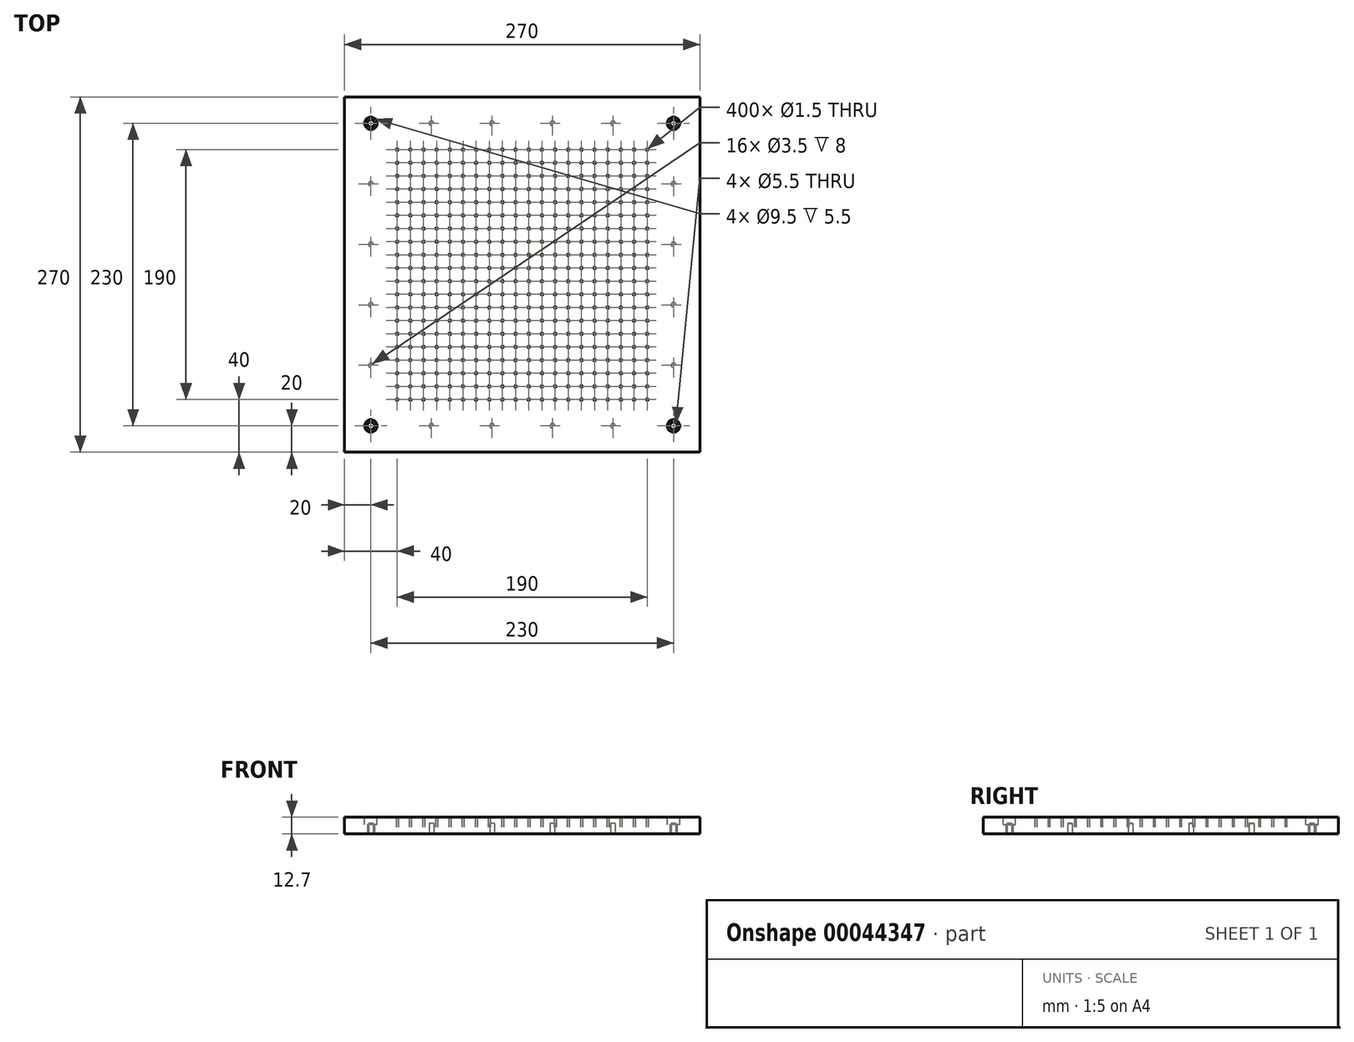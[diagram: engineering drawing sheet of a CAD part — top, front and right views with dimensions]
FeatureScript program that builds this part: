
annotation { "Feature Type Name" : "Feature", "Feature Type Description" : "" }
export const myFeature = defineFeature(function(context is Context, id is Id, definition is map)
    precondition{}
    {
        {
            var Q0;
            Q0=qCreatedBy(makeId("Top.planeOp"),FACE);
            var sketch = newSketch(context, id + "F0", { "sketchPlane" : qUnion([Q0])});
            skLineSegment(sketch, "E0.bottom", {"start": v(0, 0) * mm, "end": v(270, 0) * mm});
            skLineSegment(sketch, "E0.top", {"start": v(0, 270) * mm, "end": v(270, 270) * mm});
            skLineSegment(sketch, "E0.left", {"start": v(0, 0) * mm, "end": v(0, 270) * mm});
            skLineSegment(sketch, "E0.right", {"start": v(270, 0) * mm, "end": v(270, 270) * mm});
            skCircle(sketch, "E1", {"center": v(20, 250) * mm, "radius": 2.75 * mm});
            skCircle(sketch, "E2", {"center": v(250, 250) * mm, "radius": 2.75 * mm});
            skCircle(sketch, "E3", {"center": v(20, 20) * mm, "radius": 2.75 * mm});
            skCircle(sketch, "E4", {"center": v(250, 20) * mm, "radius": 2.75 * mm});
            skCircle(sketch, "E5", {"center": v(230, 40) * mm, "radius": 0.75 * mm});
            skCircle(sketch, "E6.0.1.0", {"center": v(230, 50) * mm, "radius": 0.75 * mm});
            skCircle(sketch, "E6.0.2.0", {"center": v(230, 60) * mm, "radius": 0.75 * mm});
            skCircle(sketch, "E6.0.3.0", {"center": v(230, 70) * mm, "radius": 0.75 * mm});
            skCircle(sketch, "E6.0.4.0", {"center": v(230, 80) * mm, "radius": 0.75 * mm});
            skCircle(sketch, "E6.0.5.0", {"center": v(230, 90) * mm, "radius": 0.75 * mm});
            skCircle(sketch, "E6.0.6.0", {"center": v(230, 100) * mm, "radius": 0.75 * mm});
            skCircle(sketch, "E6.0.7.0", {"center": v(230, 110) * mm, "radius": 0.75 * mm});
            skCircle(sketch, "E6.0.8.0", {"center": v(230, 120) * mm, "radius": 0.75 * mm});
            skCircle(sketch, "E6.0.9.0", {"center": v(230, 130) * mm, "radius": 0.75 * mm});
            skCircle(sketch, "E6.0.10.0", {"center": v(230, 140) * mm, "radius": 0.75 * mm});
            skCircle(sketch, "E6.0.11.0", {"center": v(230, 150) * mm, "radius": 0.75 * mm});
            skCircle(sketch, "E6.0.12.0", {"center": v(230, 160) * mm, "radius": 0.75 * mm});
            skCircle(sketch, "E6.0.13.0", {"center": v(230, 170) * mm, "radius": 0.75 * mm});
            skCircle(sketch, "E6.0.14.0", {"center": v(230, 180) * mm, "radius": 0.75 * mm});
            skCircle(sketch, "E6.0.15.0", {"center": v(230, 190) * mm, "radius": 0.75 * mm});
            skCircle(sketch, "E6.1.0.0", {"center": v(220, 40) * mm, "radius": 0.75 * mm});
            skCircle(sketch, "E6.1.1.0", {"center": v(220, 50) * mm, "radius": 0.75 * mm});
            skCircle(sketch, "E6.1.2.0", {"center": v(220, 60) * mm, "radius": 0.75 * mm});
            skCircle(sketch, "E6.1.3.0", {"center": v(220, 70) * mm, "radius": 0.75 * mm});
            skCircle(sketch, "E6.1.4.0", {"center": v(220, 80) * mm, "radius": 0.75 * mm});
            skCircle(sketch, "E6.1.5.0", {"center": v(220, 90) * mm, "radius": 0.75 * mm});
            skCircle(sketch, "E6.1.6.0", {"center": v(220, 100) * mm, "radius": 0.75 * mm});
            skCircle(sketch, "E6.1.7.0", {"center": v(220, 110) * mm, "radius": 0.75 * mm});
            skCircle(sketch, "E6.1.8.0", {"center": v(220, 120) * mm, "radius": 0.75 * mm});
            skCircle(sketch, "E6.1.9.0", {"center": v(220, 130) * mm, "radius": 0.75 * mm});
            skCircle(sketch, "E6.1.10.0", {"center": v(220, 140) * mm, "radius": 0.75 * mm});
            skCircle(sketch, "E6.1.11.0", {"center": v(220, 150) * mm, "radius": 0.75 * mm});
            skCircle(sketch, "E6.1.12.0", {"center": v(220, 160) * mm, "radius": 0.75 * mm});
            skCircle(sketch, "E6.1.13.0", {"center": v(220, 170) * mm, "radius": 0.75 * mm});
            skCircle(sketch, "E6.1.14.0", {"center": v(220, 180) * mm, "radius": 0.75 * mm});
            skCircle(sketch, "E6.1.15.0", {"center": v(220, 190) * mm, "radius": 0.75 * mm});
            skCircle(sketch, "E6.2.0.0", {"center": v(210, 40) * mm, "radius": 0.75 * mm});
            skCircle(sketch, "E6.2.1.0", {"center": v(210, 50) * mm, "radius": 0.75 * mm});
            skCircle(sketch, "E6.2.2.0", {"center": v(210, 60) * mm, "radius": 0.75 * mm});
            skCircle(sketch, "E6.2.3.0", {"center": v(210, 70) * mm, "radius": 0.75 * mm});
            skCircle(sketch, "E6.2.4.0", {"center": v(210, 80) * mm, "radius": 0.75 * mm});
            skCircle(sketch, "E6.2.5.0", {"center": v(210, 90) * mm, "radius": 0.75 * mm});
            skCircle(sketch, "E6.2.6.0", {"center": v(210, 100) * mm, "radius": 0.75 * mm});
            skCircle(sketch, "E6.2.7.0", {"center": v(210, 110) * mm, "radius": 0.75 * mm});
            skCircle(sketch, "E6.2.8.0", {"center": v(210, 120) * mm, "radius": 0.75 * mm});
            skCircle(sketch, "E6.2.9.0", {"center": v(210, 130) * mm, "radius": 0.75 * mm});
            skCircle(sketch, "E6.2.10.0", {"center": v(210, 140) * mm, "radius": 0.75 * mm});
            skCircle(sketch, "E6.2.11.0", {"center": v(210, 150) * mm, "radius": 0.75 * mm});
            skCircle(sketch, "E6.2.12.0", {"center": v(210, 160) * mm, "radius": 0.75 * mm});
            skCircle(sketch, "E6.2.13.0", {"center": v(210, 170) * mm, "radius": 0.75 * mm});
            skCircle(sketch, "E6.2.14.0", {"center": v(210, 180) * mm, "radius": 0.75 * mm});
            skCircle(sketch, "E6.2.15.0", {"center": v(210, 190) * mm, "radius": 0.75 * mm});
            skCircle(sketch, "E6.3.0.0", {"center": v(200, 40) * mm, "radius": 0.75 * mm});
            skCircle(sketch, "E6.3.1.0", {"center": v(200, 50) * mm, "radius": 0.75 * mm});
            skCircle(sketch, "E6.3.2.0", {"center": v(200, 60) * mm, "radius": 0.75 * mm});
            skCircle(sketch, "E6.3.3.0", {"center": v(200, 70) * mm, "radius": 0.75 * mm});
            skCircle(sketch, "E6.3.4.0", {"center": v(200, 80) * mm, "radius": 0.75 * mm});
            skCircle(sketch, "E6.3.5.0", {"center": v(200, 90) * mm, "radius": 0.75 * mm});
            skCircle(sketch, "E6.3.6.0", {"center": v(200, 100) * mm, "radius": 0.75 * mm});
            skCircle(sketch, "E6.3.7.0", {"center": v(200, 110) * mm, "radius": 0.75 * mm});
            skCircle(sketch, "E6.3.8.0", {"center": v(200, 120) * mm, "radius": 0.75 * mm});
            skCircle(sketch, "E6.3.9.0", {"center": v(200, 130) * mm, "radius": 0.75 * mm});
            skCircle(sketch, "E6.3.10.0", {"center": v(200, 140) * mm, "radius": 0.75 * mm});
            skCircle(sketch, "E6.3.11.0", {"center": v(200, 150) * mm, "radius": 0.75 * mm});
            skCircle(sketch, "E6.3.12.0", {"center": v(200, 160) * mm, "radius": 0.75 * mm});
            skCircle(sketch, "E6.3.13.0", {"center": v(200, 170) * mm, "radius": 0.75 * mm});
            skCircle(sketch, "E6.3.14.0", {"center": v(200, 180) * mm, "radius": 0.75 * mm});
            skCircle(sketch, "E6.3.15.0", {"center": v(200, 190) * mm, "radius": 0.75 * mm});
            skCircle(sketch, "E6.4.0.0", {"center": v(190, 40) * mm, "radius": 0.75 * mm});
            skCircle(sketch, "E6.4.1.0", {"center": v(190, 50) * mm, "radius": 0.75 * mm});
            skCircle(sketch, "E6.4.2.0", {"center": v(190, 60) * mm, "radius": 0.75 * mm});
            skCircle(sketch, "E6.4.3.0", {"center": v(190, 70) * mm, "radius": 0.75 * mm});
            skCircle(sketch, "E6.4.4.0", {"center": v(190, 80) * mm, "radius": 0.75 * mm});
            skCircle(sketch, "E6.4.5.0", {"center": v(190, 90) * mm, "radius": 0.75 * mm});
            skCircle(sketch, "E6.4.6.0", {"center": v(190, 100) * mm, "radius": 0.75 * mm});
            skCircle(sketch, "E6.4.7.0", {"center": v(190, 110) * mm, "radius": 0.75 * mm});
            skCircle(sketch, "E6.4.8.0", {"center": v(190, 120) * mm, "radius": 0.75 * mm});
            skCircle(sketch, "E6.4.9.0", {"center": v(190, 130) * mm, "radius": 0.75 * mm});
            skCircle(sketch, "E6.4.10.0", {"center": v(190, 140) * mm, "radius": 0.75 * mm});
            skCircle(sketch, "E6.4.11.0", {"center": v(190, 150) * mm, "radius": 0.75 * mm});
            skCircle(sketch, "E6.4.12.0", {"center": v(190, 160) * mm, "radius": 0.75 * mm});
            skCircle(sketch, "E6.4.13.0", {"center": v(190, 170) * mm, "radius": 0.75 * mm});
            skCircle(sketch, "E6.4.14.0", {"center": v(190, 180) * mm, "radius": 0.75 * mm});
            skCircle(sketch, "E6.4.15.0", {"center": v(190, 190) * mm, "radius": 0.75 * mm});
            skCircle(sketch, "E6.5.0.0", {"center": v(180, 40) * mm, "radius": 0.75 * mm});
            skCircle(sketch, "E6.5.1.0", {"center": v(180, 50) * mm, "radius": 0.75 * mm});
            skCircle(sketch, "E6.5.2.0", {"center": v(180, 60) * mm, "radius": 0.75 * mm});
            skCircle(sketch, "E6.5.3.0", {"center": v(180, 70) * mm, "radius": 0.75 * mm});
            skCircle(sketch, "E6.5.4.0", {"center": v(180, 80) * mm, "radius": 0.75 * mm});
            skCircle(sketch, "E6.5.5.0", {"center": v(180, 90) * mm, "radius": 0.75 * mm});
            skCircle(sketch, "E6.5.6.0", {"center": v(180, 100) * mm, "radius": 0.75 * mm});
            skCircle(sketch, "E6.5.7.0", {"center": v(180, 110) * mm, "radius": 0.75 * mm});
            skCircle(sketch, "E6.5.8.0", {"center": v(180, 120) * mm, "radius": 0.75 * mm});
            skCircle(sketch, "E6.5.9.0", {"center": v(180, 130) * mm, "radius": 0.75 * mm});
            skCircle(sketch, "E6.5.10.0", {"center": v(180, 140) * mm, "radius": 0.75 * mm});
            skCircle(sketch, "E6.5.11.0", {"center": v(180, 150) * mm, "radius": 0.75 * mm});
            skCircle(sketch, "E6.5.12.0", {"center": v(180, 160) * mm, "radius": 0.75 * mm});
            skCircle(sketch, "E6.5.13.0", {"center": v(180, 170) * mm, "radius": 0.75 * mm});
            skCircle(sketch, "E6.5.14.0", {"center": v(180, 180) * mm, "radius": 0.75 * mm});
            skCircle(sketch, "E6.5.15.0", {"center": v(180, 190) * mm, "radius": 0.75 * mm});
            skCircle(sketch, "E6.6.0.0", {"center": v(170, 40) * mm, "radius": 0.75 * mm});
            skCircle(sketch, "E6.6.1.0", {"center": v(170, 50) * mm, "radius": 0.75 * mm});
            skCircle(sketch, "E6.6.2.0", {"center": v(170, 60) * mm, "radius": 0.75 * mm});
            skCircle(sketch, "E6.6.3.0", {"center": v(170, 70) * mm, "radius": 0.75 * mm});
            skCircle(sketch, "E6.6.4.0", {"center": v(170, 80) * mm, "radius": 0.75 * mm});
            skCircle(sketch, "E6.6.5.0", {"center": v(170, 90) * mm, "radius": 0.75 * mm});
            skCircle(sketch, "E6.6.6.0", {"center": v(170, 100) * mm, "radius": 0.75 * mm});
            skCircle(sketch, "E6.6.7.0", {"center": v(170, 110) * mm, "radius": 0.75 * mm});
            skCircle(sketch, "E6.6.8.0", {"center": v(170, 120) * mm, "radius": 0.75 * mm});
            skCircle(sketch, "E6.6.9.0", {"center": v(170, 130) * mm, "radius": 0.75 * mm});
            skCircle(sketch, "E6.6.10.0", {"center": v(170, 140) * mm, "radius": 0.75 * mm});
            skCircle(sketch, "E6.6.11.0", {"center": v(170, 150) * mm, "radius": 0.75 * mm});
            skCircle(sketch, "E6.6.12.0", {"center": v(170, 160) * mm, "radius": 0.75 * mm});
            skCircle(sketch, "E6.6.13.0", {"center": v(170, 170) * mm, "radius": 0.75 * mm});
            skCircle(sketch, "E6.6.14.0", {"center": v(170, 180) * mm, "radius": 0.75 * mm});
            skCircle(sketch, "E6.6.15.0", {"center": v(170, 190) * mm, "radius": 0.75 * mm});
            skCircle(sketch, "E6.7.0.0", {"center": v(160, 40) * mm, "radius": 0.75 * mm});
            skCircle(sketch, "E6.7.1.0", {"center": v(160, 50) * mm, "radius": 0.75 * mm});
            skCircle(sketch, "E6.7.2.0", {"center": v(160, 60) * mm, "radius": 0.75 * mm});
            skCircle(sketch, "E6.7.3.0", {"center": v(160, 70) * mm, "radius": 0.75 * mm});
            skCircle(sketch, "E6.7.4.0", {"center": v(160, 80) * mm, "radius": 0.75 * mm});
            skCircle(sketch, "E6.7.5.0", {"center": v(160, 90) * mm, "radius": 0.75 * mm});
            skCircle(sketch, "E6.7.6.0", {"center": v(160, 100) * mm, "radius": 0.75 * mm});
            skCircle(sketch, "E6.7.7.0", {"center": v(160, 110) * mm, "radius": 0.75 * mm});
            skCircle(sketch, "E6.7.8.0", {"center": v(160, 120) * mm, "radius": 0.75 * mm});
            skCircle(sketch, "E6.7.9.0", {"center": v(160, 130) * mm, "radius": 0.75 * mm});
            skCircle(sketch, "E6.7.10.0", {"center": v(160, 140) * mm, "radius": 0.75 * mm});
            skCircle(sketch, "E6.7.11.0", {"center": v(160, 150) * mm, "radius": 0.75 * mm});
            skCircle(sketch, "E6.7.12.0", {"center": v(160, 160) * mm, "radius": 0.75 * mm});
            skCircle(sketch, "E6.7.13.0", {"center": v(160, 170) * mm, "radius": 0.75 * mm});
            skCircle(sketch, "E6.7.14.0", {"center": v(160, 180) * mm, "radius": 0.75 * mm});
            skCircle(sketch, "E6.7.15.0", {"center": v(160, 190) * mm, "radius": 0.75 * mm});
            skCircle(sketch, "E6.8.0.0", {"center": v(150, 40) * mm, "radius": 0.75 * mm});
            skCircle(sketch, "E6.8.1.0", {"center": v(150, 50) * mm, "radius": 0.75 * mm});
            skCircle(sketch, "E6.8.2.0", {"center": v(150, 60) * mm, "radius": 0.75 * mm});
            skCircle(sketch, "E6.8.3.0", {"center": v(150, 70) * mm, "radius": 0.75 * mm});
            skCircle(sketch, "E6.8.4.0", {"center": v(150, 80) * mm, "radius": 0.75 * mm});
            skCircle(sketch, "E6.8.5.0", {"center": v(150, 90) * mm, "radius": 0.75 * mm});
            skCircle(sketch, "E6.8.6.0", {"center": v(150, 100) * mm, "radius": 0.75 * mm});
            skCircle(sketch, "E6.8.7.0", {"center": v(150, 110) * mm, "radius": 0.75 * mm});
            skCircle(sketch, "E6.8.8.0", {"center": v(150, 120) * mm, "radius": 0.75 * mm});
            skCircle(sketch, "E6.8.9.0", {"center": v(150, 130) * mm, "radius": 0.75 * mm});
            skCircle(sketch, "E6.8.10.0", {"center": v(150, 140) * mm, "radius": 0.75 * mm});
            skCircle(sketch, "E6.8.11.0", {"center": v(150, 150) * mm, "radius": 0.75 * mm});
            skCircle(sketch, "E6.8.12.0", {"center": v(150, 160) * mm, "radius": 0.75 * mm});
            skCircle(sketch, "E6.8.13.0", {"center": v(150, 170) * mm, "radius": 0.75 * mm});
            skCircle(sketch, "E6.8.14.0", {"center": v(150, 180) * mm, "radius": 0.75 * mm});
            skCircle(sketch, "E6.8.15.0", {"center": v(150, 190) * mm, "radius": 0.75 * mm});
            skCircle(sketch, "E6.9.0.0", {"center": v(140, 40) * mm, "radius": 0.75 * mm});
            skCircle(sketch, "E6.9.1.0", {"center": v(140, 50) * mm, "radius": 0.75 * mm});
            skCircle(sketch, "E6.9.2.0", {"center": v(140, 60) * mm, "radius": 0.75 * mm});
            skCircle(sketch, "E6.9.3.0", {"center": v(140, 70) * mm, "radius": 0.75 * mm});
            skCircle(sketch, "E6.9.4.0", {"center": v(140, 80) * mm, "radius": 0.75 * mm});
            skCircle(sketch, "E6.9.5.0", {"center": v(140, 90) * mm, "radius": 0.75 * mm});
            skCircle(sketch, "E6.9.6.0", {"center": v(140, 100) * mm, "radius": 0.75 * mm});
            skCircle(sketch, "E6.9.7.0", {"center": v(140, 110) * mm, "radius": 0.75 * mm});
            skCircle(sketch, "E6.9.8.0", {"center": v(140, 120) * mm, "radius": 0.75 * mm});
            skCircle(sketch, "E6.9.9.0", {"center": v(140, 130) * mm, "radius": 0.75 * mm});
            skCircle(sketch, "E6.9.10.0", {"center": v(140, 140) * mm, "radius": 0.75 * mm});
            skCircle(sketch, "E6.9.11.0", {"center": v(140, 150) * mm, "radius": 0.75 * mm});
            skCircle(sketch, "E6.9.12.0", {"center": v(140, 160) * mm, "radius": 0.75 * mm});
            skCircle(sketch, "E6.9.13.0", {"center": v(140, 170) * mm, "radius": 0.75 * mm});
            skCircle(sketch, "E6.9.14.0", {"center": v(140, 180) * mm, "radius": 0.75 * mm});
            skCircle(sketch, "E6.9.15.0", {"center": v(140, 190) * mm, "radius": 0.75 * mm});
            skCircle(sketch, "E6.10.0.0", {"center": v(130, 40) * mm, "radius": 0.75 * mm});
            skCircle(sketch, "E6.10.1.0", {"center": v(130, 50) * mm, "radius": 0.75 * mm});
            skCircle(sketch, "E6.10.2.0", {"center": v(130, 60) * mm, "radius": 0.75 * mm});
            skCircle(sketch, "E6.10.3.0", {"center": v(130, 70) * mm, "radius": 0.75 * mm});
            skCircle(sketch, "E6.10.4.0", {"center": v(130, 80) * mm, "radius": 0.75 * mm});
            skCircle(sketch, "E6.10.5.0", {"center": v(130, 90) * mm, "radius": 0.75 * mm});
            skCircle(sketch, "E6.10.6.0", {"center": v(130, 100) * mm, "radius": 0.75 * mm});
            skCircle(sketch, "E6.10.7.0", {"center": v(130, 110) * mm, "radius": 0.75 * mm});
            skCircle(sketch, "E6.10.8.0", {"center": v(130, 120) * mm, "radius": 0.75 * mm});
            skCircle(sketch, "E6.10.9.0", {"center": v(130, 130) * mm, "radius": 0.75 * mm});
            skCircle(sketch, "E6.10.10.0", {"center": v(130, 140) * mm, "radius": 0.75 * mm});
            skCircle(sketch, "E6.10.11.0", {"center": v(130, 150) * mm, "radius": 0.75 * mm});
            skCircle(sketch, "E6.10.12.0", {"center": v(130, 160) * mm, "radius": 0.75 * mm});
            skCircle(sketch, "E6.10.13.0", {"center": v(130, 170) * mm, "radius": 0.75 * mm});
            skCircle(sketch, "E6.10.14.0", {"center": v(130, 180) * mm, "radius": 0.75 * mm});
            skCircle(sketch, "E6.10.15.0", {"center": v(130, 190) * mm, "radius": 0.75 * mm});
            skCircle(sketch, "E6.11.0.0", {"center": v(120, 40) * mm, "radius": 0.75 * mm});
            skCircle(sketch, "E6.11.1.0", {"center": v(120, 50) * mm, "radius": 0.75 * mm});
            skCircle(sketch, "E6.11.2.0", {"center": v(120, 60) * mm, "radius": 0.75 * mm});
            skCircle(sketch, "E6.11.3.0", {"center": v(120, 70) * mm, "radius": 0.75 * mm});
            skCircle(sketch, "E6.11.4.0", {"center": v(120, 80) * mm, "radius": 0.75 * mm});
            skCircle(sketch, "E6.11.5.0", {"center": v(120, 90) * mm, "radius": 0.75 * mm});
            skCircle(sketch, "E6.11.6.0", {"center": v(120, 100) * mm, "radius": 0.75 * mm});
            skCircle(sketch, "E6.11.7.0", {"center": v(120, 110) * mm, "radius": 0.75 * mm});
            skCircle(sketch, "E6.11.8.0", {"center": v(120, 120) * mm, "radius": 0.75 * mm});
            skCircle(sketch, "E6.11.9.0", {"center": v(120, 130) * mm, "radius": 0.75 * mm});
            skCircle(sketch, "E6.11.10.0", {"center": v(120, 140) * mm, "radius": 0.75 * mm});
            skCircle(sketch, "E6.11.11.0", {"center": v(120, 150) * mm, "radius": 0.75 * mm});
            skCircle(sketch, "E6.11.12.0", {"center": v(120, 160) * mm, "radius": 0.75 * mm});
            skCircle(sketch, "E6.11.13.0", {"center": v(120, 170) * mm, "radius": 0.75 * mm});
            skCircle(sketch, "E6.11.14.0", {"center": v(120, 180) * mm, "radius": 0.75 * mm});
            skCircle(sketch, "E6.11.15.0", {"center": v(120, 190) * mm, "radius": 0.75 * mm});
            skCircle(sketch, "E6.12.0.0", {"center": v(110, 40) * mm, "radius": 0.75 * mm});
            skCircle(sketch, "E6.12.1.0", {"center": v(110, 50) * mm, "radius": 0.75 * mm});
            skCircle(sketch, "E6.12.2.0", {"center": v(110, 60) * mm, "radius": 0.75 * mm});
            skCircle(sketch, "E6.12.3.0", {"center": v(110, 70) * mm, "radius": 0.75 * mm});
            skCircle(sketch, "E6.12.4.0", {"center": v(110, 80) * mm, "radius": 0.75 * mm});
            skCircle(sketch, "E6.12.5.0", {"center": v(110, 90) * mm, "radius": 0.75 * mm});
            skCircle(sketch, "E6.12.6.0", {"center": v(110, 100) * mm, "radius": 0.75 * mm});
            skCircle(sketch, "E6.12.7.0", {"center": v(110, 110) * mm, "radius": 0.75 * mm});
            skCircle(sketch, "E6.12.8.0", {"center": v(110, 120) * mm, "radius": 0.75 * mm});
            skCircle(sketch, "E6.12.9.0", {"center": v(110, 130) * mm, "radius": 0.75 * mm});
            skCircle(sketch, "E6.12.10.0", {"center": v(110, 140) * mm, "radius": 0.75 * mm});
            skCircle(sketch, "E6.12.11.0", {"center": v(110, 150) * mm, "radius": 0.75 * mm});
            skCircle(sketch, "E6.12.12.0", {"center": v(110, 160) * mm, "radius": 0.75 * mm});
            skCircle(sketch, "E6.12.13.0", {"center": v(110, 170) * mm, "radius": 0.75 * mm});
            skCircle(sketch, "E6.12.14.0", {"center": v(110, 180) * mm, "radius": 0.75 * mm});
            skCircle(sketch, "E6.12.15.0", {"center": v(110, 190) * mm, "radius": 0.75 * mm});
            skCircle(sketch, "E6.13.0.0", {"center": v(100, 40) * mm, "radius": 0.75 * mm});
            skCircle(sketch, "E6.13.1.0", {"center": v(100, 50) * mm, "radius": 0.75 * mm});
            skCircle(sketch, "E6.13.2.0", {"center": v(100, 60) * mm, "radius": 0.75 * mm});
            skCircle(sketch, "E6.13.3.0", {"center": v(100, 70) * mm, "radius": 0.75 * mm});
            skCircle(sketch, "E6.13.4.0", {"center": v(100, 80) * mm, "radius": 0.75 * mm});
            skCircle(sketch, "E6.13.5.0", {"center": v(100, 90) * mm, "radius": 0.75 * mm});
            skCircle(sketch, "E6.13.6.0", {"center": v(100, 100) * mm, "radius": 0.75 * mm});
            skCircle(sketch, "E6.13.7.0", {"center": v(100, 110) * mm, "radius": 0.75 * mm});
            skCircle(sketch, "E6.13.8.0", {"center": v(100, 120) * mm, "radius": 0.75 * mm});
            skCircle(sketch, "E6.13.9.0", {"center": v(100, 130) * mm, "radius": 0.75 * mm});
            skCircle(sketch, "E6.13.10.0", {"center": v(100, 140) * mm, "radius": 0.75 * mm});
            skCircle(sketch, "E6.13.11.0", {"center": v(100, 150) * mm, "radius": 0.75 * mm});
            skCircle(sketch, "E6.13.12.0", {"center": v(100, 160) * mm, "radius": 0.75 * mm});
            skCircle(sketch, "E6.13.13.0", {"center": v(100, 170) * mm, "radius": 0.75 * mm});
            skCircle(sketch, "E6.13.14.0", {"center": v(100, 180) * mm, "radius": 0.75 * mm});
            skCircle(sketch, "E6.13.15.0", {"center": v(100, 190) * mm, "radius": 0.75 * mm});
            skCircle(sketch, "E6.14.0.0", {"center": v(90, 40) * mm, "radius": 0.75 * mm});
            skCircle(sketch, "E6.14.1.0", {"center": v(90, 50) * mm, "radius": 0.75 * mm});
            skCircle(sketch, "E6.14.2.0", {"center": v(90, 60) * mm, "radius": 0.75 * mm});
            skCircle(sketch, "E6.14.3.0", {"center": v(90, 70) * mm, "radius": 0.75 * mm});
            skCircle(sketch, "E6.14.4.0", {"center": v(90, 80) * mm, "radius": 0.75 * mm});
            skCircle(sketch, "E6.14.5.0", {"center": v(90, 90) * mm, "radius": 0.75 * mm});
            skCircle(sketch, "E6.14.6.0", {"center": v(90, 100) * mm, "radius": 0.75 * mm});
            skCircle(sketch, "E6.14.7.0", {"center": v(90, 110) * mm, "radius": 0.75 * mm});
            skCircle(sketch, "E6.14.8.0", {"center": v(90, 120) * mm, "radius": 0.75 * mm});
            skCircle(sketch, "E6.14.9.0", {"center": v(90, 130) * mm, "radius": 0.75 * mm});
            skCircle(sketch, "E6.14.10.0", {"center": v(90, 140) * mm, "radius": 0.75 * mm});
            skCircle(sketch, "E6.14.11.0", {"center": v(90, 150) * mm, "radius": 0.75 * mm});
            skCircle(sketch, "E6.14.12.0", {"center": v(90, 160) * mm, "radius": 0.75 * mm});
            skCircle(sketch, "E6.14.13.0", {"center": v(90, 170) * mm, "radius": 0.75 * mm});
            skCircle(sketch, "E6.14.14.0", {"center": v(90, 180) * mm, "radius": 0.75 * mm});
            skCircle(sketch, "E6.14.15.0", {"center": v(90, 190) * mm, "radius": 0.75 * mm});
            skCircle(sketch, "E6.15.0.0", {"center": v(80, 40) * mm, "radius": 0.75 * mm});
            skCircle(sketch, "E6.15.1.0", {"center": v(80, 50) * mm, "radius": 0.75 * mm});
            skCircle(sketch, "E6.15.2.0", {"center": v(80, 60) * mm, "radius": 0.75 * mm});
            skCircle(sketch, "E6.15.3.0", {"center": v(80, 70) * mm, "radius": 0.75 * mm});
            skCircle(sketch, "E6.15.4.0", {"center": v(80, 80) * mm, "radius": 0.75 * mm});
            skCircle(sketch, "E6.15.5.0", {"center": v(80, 90) * mm, "radius": 0.75 * mm});
            skCircle(sketch, "E6.15.6.0", {"center": v(80, 100) * mm, "radius": 0.75 * mm});
            skCircle(sketch, "E6.15.7.0", {"center": v(80, 110) * mm, "radius": 0.75 * mm});
            skCircle(sketch, "E6.15.8.0", {"center": v(80, 120) * mm, "radius": 0.75 * mm});
            skCircle(sketch, "E6.15.9.0", {"center": v(80, 130) * mm, "radius": 0.75 * mm});
            skCircle(sketch, "E6.15.10.0", {"center": v(80, 140) * mm, "radius": 0.75 * mm});
            skCircle(sketch, "E6.15.11.0", {"center": v(80, 150) * mm, "radius": 0.75 * mm});
            skCircle(sketch, "E6.15.12.0", {"center": v(80, 160) * mm, "radius": 0.75 * mm});
            skCircle(sketch, "E6.15.13.0", {"center": v(80, 170) * mm, "radius": 0.75 * mm});
            skCircle(sketch, "E6.15.14.0", {"center": v(80, 180) * mm, "radius": 0.75 * mm});
            skCircle(sketch, "E6.15.15.0", {"center": v(80, 190) * mm, "radius": 0.75 * mm});
            skLineSegment(sketch, "E6.direction1", {"start": v(230, 40) * mm, "end": v(220, 40) * mm, "construction": true});
            skLineSegment(sketch, "E6.direction2", {"start": v(230, 40) * mm, "end": v(230, 50) * mm, "construction": true});
            skCircle(sketch, "E7.0.0.16", {"center": v(230, 200) * mm, "radius": 0.75 * mm});
            skCircle(sketch, "E7.0.0.17", {"center": v(230, 210) * mm, "radius": 0.75 * mm});
            skCircle(sketch, "E7.0.0.18", {"center": v(230, 220) * mm, "radius": 0.75 * mm});
            skCircle(sketch, "E7.0.0.19", {"center": v(230, 230) * mm, "radius": 0.75 * mm});
            skCircle(sketch, "E7.0.1.16", {"center": v(220, 200) * mm, "radius": 0.75 * mm});
            skCircle(sketch, "E7.0.1.17", {"center": v(220, 210) * mm, "radius": 0.75 * mm});
            skCircle(sketch, "E7.0.1.18", {"center": v(220, 220) * mm, "radius": 0.75 * mm});
            skCircle(sketch, "E7.0.1.19", {"center": v(220, 230) * mm, "radius": 0.75 * mm});
            skCircle(sketch, "E7.0.2.16", {"center": v(210, 200) * mm, "radius": 0.75 * mm});
            skCircle(sketch, "E7.0.2.17", {"center": v(210, 210) * mm, "radius": 0.75 * mm});
            skCircle(sketch, "E7.0.2.18", {"center": v(210, 220) * mm, "radius": 0.75 * mm});
            skCircle(sketch, "E7.0.2.19", {"center": v(210, 230) * mm, "radius": 0.75 * mm});
            skCircle(sketch, "E7.0.3.16", {"center": v(200, 200) * mm, "radius": 0.75 * mm});
            skCircle(sketch, "E7.0.3.17", {"center": v(200, 210) * mm, "radius": 0.75 * mm});
            skCircle(sketch, "E7.0.3.18", {"center": v(200, 220) * mm, "radius": 0.75 * mm});
            skCircle(sketch, "E7.0.3.19", {"center": v(200, 230) * mm, "radius": 0.75 * mm});
            skCircle(sketch, "E7.0.4.16", {"center": v(190, 200) * mm, "radius": 0.75 * mm});
            skCircle(sketch, "E7.0.4.17", {"center": v(190, 210) * mm, "radius": 0.75 * mm});
            skCircle(sketch, "E7.0.4.18", {"center": v(190, 220) * mm, "radius": 0.75 * mm});
            skCircle(sketch, "E7.0.4.19", {"center": v(190, 230) * mm, "radius": 0.75 * mm});
            skCircle(sketch, "E7.0.5.16", {"center": v(180, 200) * mm, "radius": 0.75 * mm});
            skCircle(sketch, "E7.0.5.17", {"center": v(180, 210) * mm, "radius": 0.75 * mm});
            skCircle(sketch, "E7.0.5.18", {"center": v(180, 220) * mm, "radius": 0.75 * mm});
            skCircle(sketch, "E7.0.5.19", {"center": v(180, 230) * mm, "radius": 0.75 * mm});
            skCircle(sketch, "E7.0.6.16", {"center": v(170, 200) * mm, "radius": 0.75 * mm});
            skCircle(sketch, "E7.0.6.17", {"center": v(170, 210) * mm, "radius": 0.75 * mm});
            skCircle(sketch, "E7.0.6.18", {"center": v(170, 220) * mm, "radius": 0.75 * mm});
            skCircle(sketch, "E7.0.6.19", {"center": v(170, 230) * mm, "radius": 0.75 * mm});
            skCircle(sketch, "E7.0.7.16", {"center": v(160, 200) * mm, "radius": 0.75 * mm});
            skCircle(sketch, "E7.0.7.17", {"center": v(160, 210) * mm, "radius": 0.75 * mm});
            skCircle(sketch, "E7.0.7.18", {"center": v(160, 220) * mm, "radius": 0.75 * mm});
            skCircle(sketch, "E7.0.7.19", {"center": v(160, 230) * mm, "radius": 0.75 * mm});
            skCircle(sketch, "E7.0.8.16", {"center": v(150, 200) * mm, "radius": 0.75 * mm});
            skCircle(sketch, "E7.0.8.17", {"center": v(150, 210) * mm, "radius": 0.75 * mm});
            skCircle(sketch, "E7.0.8.18", {"center": v(150, 220) * mm, "radius": 0.75 * mm});
            skCircle(sketch, "E7.0.8.19", {"center": v(150, 230) * mm, "radius": 0.75 * mm});
            skCircle(sketch, "E7.0.9.16", {"center": v(140, 200) * mm, "radius": 0.75 * mm});
            skCircle(sketch, "E7.0.9.17", {"center": v(140, 210) * mm, "radius": 0.75 * mm});
            skCircle(sketch, "E7.0.9.18", {"center": v(140, 220) * mm, "radius": 0.75 * mm});
            skCircle(sketch, "E7.0.9.19", {"center": v(140, 230) * mm, "radius": 0.75 * mm});
            skCircle(sketch, "E7.0.10.16", {"center": v(130, 200) * mm, "radius": 0.75 * mm});
            skCircle(sketch, "E7.0.10.17", {"center": v(130, 210) * mm, "radius": 0.75 * mm});
            skCircle(sketch, "E7.0.10.18", {"center": v(130, 220) * mm, "radius": 0.75 * mm});
            skCircle(sketch, "E7.0.10.19", {"center": v(130, 230) * mm, "radius": 0.75 * mm});
            skCircle(sketch, "E7.0.11.16", {"center": v(120, 200) * mm, "radius": 0.75 * mm});
            skCircle(sketch, "E7.0.11.17", {"center": v(120, 210) * mm, "radius": 0.75 * mm});
            skCircle(sketch, "E7.0.11.18", {"center": v(120, 220) * mm, "radius": 0.75 * mm});
            skCircle(sketch, "E7.0.11.19", {"center": v(120, 230) * mm, "radius": 0.75 * mm});
            skCircle(sketch, "E7.0.12.16", {"center": v(110, 200) * mm, "radius": 0.75 * mm});
            skCircle(sketch, "E7.0.12.17", {"center": v(110, 210) * mm, "radius": 0.75 * mm});
            skCircle(sketch, "E7.0.12.18", {"center": v(110, 220) * mm, "radius": 0.75 * mm});
            skCircle(sketch, "E7.0.12.19", {"center": v(110, 230) * mm, "radius": 0.75 * mm});
            skCircle(sketch, "E7.0.13.16", {"center": v(100, 200) * mm, "radius": 0.75 * mm});
            skCircle(sketch, "E7.0.13.17", {"center": v(100, 210) * mm, "radius": 0.75 * mm});
            skCircle(sketch, "E7.0.13.18", {"center": v(100, 220) * mm, "radius": 0.75 * mm});
            skCircle(sketch, "E7.0.13.19", {"center": v(100, 230) * mm, "radius": 0.75 * mm});
            skCircle(sketch, "E7.0.14.16", {"center": v(90, 200) * mm, "radius": 0.75 * mm});
            skCircle(sketch, "E7.0.14.17", {"center": v(90, 210) * mm, "radius": 0.75 * mm});
            skCircle(sketch, "E7.0.14.18", {"center": v(90, 220) * mm, "radius": 0.75 * mm});
            skCircle(sketch, "E7.0.14.19", {"center": v(90, 230) * mm, "radius": 0.75 * mm});
            skCircle(sketch, "E7.0.15.16", {"center": v(80, 200) * mm, "radius": 0.75 * mm});
            skCircle(sketch, "E7.0.15.17", {"center": v(80, 210) * mm, "radius": 0.75 * mm});
            skCircle(sketch, "E7.0.15.18", {"center": v(80, 220) * mm, "radius": 0.75 * mm});
            skCircle(sketch, "E7.0.15.19", {"center": v(80, 230) * mm, "radius": 0.75 * mm});
            skCircle(sketch, "E8.0.16.0", {"center": v(70, 40) * mm, "radius": 0.75 * mm});
            skCircle(sketch, "E8.0.16.1", {"center": v(70, 50) * mm, "radius": 0.75 * mm});
            skCircle(sketch, "E8.0.16.2", {"center": v(70, 60) * mm, "radius": 0.75 * mm});
            skCircle(sketch, "E8.0.16.3", {"center": v(70, 70) * mm, "radius": 0.75 * mm});
            skCircle(sketch, "E8.0.16.4", {"center": v(70, 80) * mm, "radius": 0.75 * mm});
            skCircle(sketch, "E8.0.16.5", {"center": v(70, 90) * mm, "radius": 0.75 * mm});
            skCircle(sketch, "E8.0.16.6", {"center": v(70, 100) * mm, "radius": 0.75 * mm});
            skCircle(sketch, "E8.0.16.7", {"center": v(70, 110) * mm, "radius": 0.75 * mm});
            skCircle(sketch, "E8.0.16.8", {"center": v(70, 120) * mm, "radius": 0.75 * mm});
            skCircle(sketch, "E8.0.16.9", {"center": v(70, 130) * mm, "radius": 0.75 * mm});
            skCircle(sketch, "E8.0.16.10", {"center": v(70, 140) * mm, "radius": 0.75 * mm});
            skCircle(sketch, "E8.0.16.11", {"center": v(70, 150) * mm, "radius": 0.75 * mm});
            skCircle(sketch, "E8.0.16.12", {"center": v(70, 160) * mm, "radius": 0.75 * mm});
            skCircle(sketch, "E8.0.16.13", {"center": v(70, 170) * mm, "radius": 0.75 * mm});
            skCircle(sketch, "E8.0.16.14", {"center": v(70, 180) * mm, "radius": 0.75 * mm});
            skCircle(sketch, "E8.0.16.15", {"center": v(70, 190) * mm, "radius": 0.75 * mm});
            skCircle(sketch, "E8.0.16.16", {"center": v(70, 200) * mm, "radius": 0.75 * mm});
            skCircle(sketch, "E8.0.16.17", {"center": v(70, 210) * mm, "radius": 0.75 * mm});
            skCircle(sketch, "E8.0.16.18", {"center": v(70, 220) * mm, "radius": 0.75 * mm});
            skCircle(sketch, "E8.0.16.19", {"center": v(70, 230) * mm, "radius": 0.75 * mm});
            skCircle(sketch, "E8.0.17.0", {"center": v(60, 40) * mm, "radius": 0.75 * mm});
            skCircle(sketch, "E8.0.17.1", {"center": v(60, 50) * mm, "radius": 0.75 * mm});
            skCircle(sketch, "E8.0.17.2", {"center": v(60, 60) * mm, "radius": 0.75 * mm});
            skCircle(sketch, "E8.0.17.3", {"center": v(60, 70) * mm, "radius": 0.75 * mm});
            skCircle(sketch, "E8.0.17.4", {"center": v(60, 80) * mm, "radius": 0.75 * mm});
            skCircle(sketch, "E8.0.17.5", {"center": v(60, 90) * mm, "radius": 0.75 * mm});
            skCircle(sketch, "E8.0.17.6", {"center": v(60, 100) * mm, "radius": 0.75 * mm});
            skCircle(sketch, "E8.0.17.7", {"center": v(60, 110) * mm, "radius": 0.75 * mm});
            skCircle(sketch, "E8.0.17.8", {"center": v(60, 120) * mm, "radius": 0.75 * mm});
            skCircle(sketch, "E8.0.17.9", {"center": v(60, 130) * mm, "radius": 0.75 * mm});
            skCircle(sketch, "E8.0.17.10", {"center": v(60, 140) * mm, "radius": 0.75 * mm});
            skCircle(sketch, "E8.0.17.11", {"center": v(60, 150) * mm, "radius": 0.75 * mm});
            skCircle(sketch, "E8.0.17.12", {"center": v(60, 160) * mm, "radius": 0.75 * mm});
            skCircle(sketch, "E8.0.17.13", {"center": v(60, 170) * mm, "radius": 0.75 * mm});
            skCircle(sketch, "E8.0.17.14", {"center": v(60, 180) * mm, "radius": 0.75 * mm});
            skCircle(sketch, "E8.0.17.15", {"center": v(60, 190) * mm, "radius": 0.75 * mm});
            skCircle(sketch, "E8.0.17.16", {"center": v(60, 200) * mm, "radius": 0.75 * mm});
            skCircle(sketch, "E8.0.17.17", {"center": v(60, 210) * mm, "radius": 0.75 * mm});
            skCircle(sketch, "E8.0.17.18", {"center": v(60, 220) * mm, "radius": 0.75 * mm});
            skCircle(sketch, "E8.0.17.19", {"center": v(60, 230) * mm, "radius": 0.75 * mm});
            skCircle(sketch, "E8.0.18.0", {"center": v(50, 40) * mm, "radius": 0.75 * mm});
            skCircle(sketch, "E8.0.18.1", {"center": v(50, 50) * mm, "radius": 0.75 * mm});
            skCircle(sketch, "E8.0.18.2", {"center": v(50, 60) * mm, "radius": 0.75 * mm});
            skCircle(sketch, "E8.0.18.3", {"center": v(50, 70) * mm, "radius": 0.75 * mm});
            skCircle(sketch, "E8.0.18.4", {"center": v(50, 80) * mm, "radius": 0.75 * mm});
            skCircle(sketch, "E8.0.18.5", {"center": v(50, 90) * mm, "radius": 0.75 * mm});
            skCircle(sketch, "E8.0.18.6", {"center": v(50, 100) * mm, "radius": 0.75 * mm});
            skCircle(sketch, "E8.0.18.7", {"center": v(50, 110) * mm, "radius": 0.75 * mm});
            skCircle(sketch, "E8.0.18.8", {"center": v(50, 120) * mm, "radius": 0.75 * mm});
            skCircle(sketch, "E8.0.18.9", {"center": v(50, 130) * mm, "radius": 0.75 * mm});
            skCircle(sketch, "E8.0.18.10", {"center": v(50, 140) * mm, "radius": 0.75 * mm});
            skCircle(sketch, "E8.0.18.11", {"center": v(50, 150) * mm, "radius": 0.75 * mm});
            skCircle(sketch, "E8.0.18.12", {"center": v(50, 160) * mm, "radius": 0.75 * mm});
            skCircle(sketch, "E8.0.18.13", {"center": v(50, 170) * mm, "radius": 0.75 * mm});
            skCircle(sketch, "E8.0.18.14", {"center": v(50, 180) * mm, "radius": 0.75 * mm});
            skCircle(sketch, "E8.0.18.15", {"center": v(50, 190) * mm, "radius": 0.75 * mm});
            skCircle(sketch, "E8.0.18.16", {"center": v(50, 200) * mm, "radius": 0.75 * mm});
            skCircle(sketch, "E8.0.18.17", {"center": v(50, 210) * mm, "radius": 0.75 * mm});
            skCircle(sketch, "E8.0.18.18", {"center": v(50, 220) * mm, "radius": 0.75 * mm});
            skCircle(sketch, "E8.0.18.19", {"center": v(50, 230) * mm, "radius": 0.75 * mm});
            skCircle(sketch, "E8.0.19.0", {"center": v(40, 40) * mm, "radius": 0.75 * mm});
            skCircle(sketch, "E8.0.19.1", {"center": v(40, 50) * mm, "radius": 0.75 * mm});
            skCircle(sketch, "E8.0.19.2", {"center": v(40, 60) * mm, "radius": 0.75 * mm});
            skCircle(sketch, "E8.0.19.3", {"center": v(40, 70) * mm, "radius": 0.75 * mm});
            skCircle(sketch, "E8.0.19.4", {"center": v(40, 80) * mm, "radius": 0.75 * mm});
            skCircle(sketch, "E8.0.19.5", {"center": v(40, 90) * mm, "radius": 0.75 * mm});
            skCircle(sketch, "E8.0.19.6", {"center": v(40, 100) * mm, "radius": 0.75 * mm});
            skCircle(sketch, "E8.0.19.7", {"center": v(40, 110) * mm, "radius": 0.75 * mm});
            skCircle(sketch, "E8.0.19.8", {"center": v(40, 120) * mm, "radius": 0.75 * mm});
            skCircle(sketch, "E8.0.19.9", {"center": v(40, 130) * mm, "radius": 0.75 * mm});
            skCircle(sketch, "E8.0.19.10", {"center": v(40, 140) * mm, "radius": 0.75 * mm});
            skCircle(sketch, "E8.0.19.11", {"center": v(40, 150) * mm, "radius": 0.75 * mm});
            skCircle(sketch, "E8.0.19.12", {"center": v(40, 160) * mm, "radius": 0.75 * mm});
            skCircle(sketch, "E8.0.19.13", {"center": v(40, 170) * mm, "radius": 0.75 * mm});
            skCircle(sketch, "E8.0.19.14", {"center": v(40, 180) * mm, "radius": 0.75 * mm});
            skCircle(sketch, "E8.0.19.15", {"center": v(40, 190) * mm, "radius": 0.75 * mm});
            skCircle(sketch, "E8.0.19.16", {"center": v(40, 200) * mm, "radius": 0.75 * mm});
            skCircle(sketch, "E8.0.19.17", {"center": v(40, 210) * mm, "radius": 0.75 * mm});
            skCircle(sketch, "E8.0.19.18", {"center": v(40, 220) * mm, "radius": 0.75 * mm});
            skCircle(sketch, "E8.0.19.19", {"center": v(40, 230) * mm, "radius": 0.75 * mm});
            skSolve(sketch);
        }
        {
            var Q0;
            Q0=makeQuery(id+"F0.imprint","IMPRINT",FACE,{"disambiguationData":[TD([[makeQuery(id+"F0.imprint","IMPRINT",EDGE,{"derivedFrom":sQuery(id+"F0.wireOp",EDGE,"E0.bottom")}),1.0]])]});
            extrude(context, id + "F1", {"entities" : qUnion([Q0]), "depth" : 12.7 * mm});
        }
        {
            var Q0;
            Q0=makeQuery(id+"F1.opExtrude","CAP_FACE",FACE,{"disambiguationData":[OSD([sQuery(id+"F0.wireOp",EDGE,"E0.bottom"),sQuery(id+"F0.wireOp",EDGE,"E0.top"),sQuery(id+"F0.wireOp",EDGE,"E0.left"),sQuery(id+"F0.wireOp",EDGE,"E0.right"),sQuery(id+"F0.wireOp",EDGE,"E1"),sQuery(id+"F0.wireOp",EDGE,"E2"),sQuery(id+"F0.wireOp",EDGE,"E3"),sQuery(id+"F0.wireOp",EDGE,"E4"),sQuery(id+"F0.wireOp",EDGE,"E5"),sQuery(id+"F0.wireOp",EDGE,"E6.0.1.0"),sQuery(id+"F0.wireOp",EDGE,"E6.0.2.0"),sQuery(id+"F0.wireOp",EDGE,"E6.0.3.0"),sQuery(id+"F0.wireOp",EDGE,"E6.0.4.0"),sQuery(id+"F0.wireOp",EDGE,"E6.0.5.0"),sQuery(id+"F0.wireOp",EDGE,"E6.0.6.0"),sQuery(id+"F0.wireOp",EDGE,"E6.0.7.0"),sQuery(id+"F0.wireOp",EDGE,"E6.0.8.0"),sQuery(id+"F0.wireOp",EDGE,"E6.0.9.0"),sQuery(id+"F0.wireOp",EDGE,"E6.0.10.0"),sQuery(id+"F0.wireOp",EDGE,"E6.0.11.0"),sQuery(id+"F0.wireOp",EDGE,"E6.0.12.0"),sQuery(id+"F0.wireOp",EDGE,"E6.0.13.0"),sQuery(id+"F0.wireOp",EDGE,"E6.0.14.0"),sQuery(id+"F0.wireOp",EDGE,"E6.0.15.0"),sQuery(id+"F0.wireOp",EDGE,"E6.1.0.0"),sQuery(id+"F0.wireOp",EDGE,"E6.1.1.0"),sQuery(id+"F0.wireOp",EDGE,"E6.1.2.0"),sQuery(id+"F0.wireOp",EDGE,"E6.1.3.0"),sQuery(id+"F0.wireOp",EDGE,"E6.1.4.0"),sQuery(id+"F0.wireOp",EDGE,"E6.1.5.0"),sQuery(id+"F0.wireOp",EDGE,"E6.1.6.0"),sQuery(id+"F0.wireOp",EDGE,"E6.1.7.0"),sQuery(id+"F0.wireOp",EDGE,"E6.1.8.0"),sQuery(id+"F0.wireOp",EDGE,"E6.1.9.0"),sQuery(id+"F0.wireOp",EDGE,"E6.1.10.0"),sQuery(id+"F0.wireOp",EDGE,"E6.1.11.0"),sQuery(id+"F0.wireOp",EDGE,"E6.1.12.0"),sQuery(id+"F0.wireOp",EDGE,"E6.1.13.0"),sQuery(id+"F0.wireOp",EDGE,"E6.1.14.0"),sQuery(id+"F0.wireOp",EDGE,"E6.1.15.0"),sQuery(id+"F0.wireOp",EDGE,"E6.2.0.0"),sQuery(id+"F0.wireOp",EDGE,"E6.2.1.0"),sQuery(id+"F0.wireOp",EDGE,"E6.2.2.0"),sQuery(id+"F0.wireOp",EDGE,"E6.2.3.0"),sQuery(id+"F0.wireOp",EDGE,"E6.2.4.0"),sQuery(id+"F0.wireOp",EDGE,"E6.2.5.0"),sQuery(id+"F0.wireOp",EDGE,"E6.2.6.0"),sQuery(id+"F0.wireOp",EDGE,"E6.2.7.0"),sQuery(id+"F0.wireOp",EDGE,"E6.2.8.0"),sQuery(id+"F0.wireOp",EDGE,"E6.2.9.0"),sQuery(id+"F0.wireOp",EDGE,"E6.2.10.0"),sQuery(id+"F0.wireOp",EDGE,"E6.2.11.0"),sQuery(id+"F0.wireOp",EDGE,"E6.2.12.0"),sQuery(id+"F0.wireOp",EDGE,"E6.2.13.0"),sQuery(id+"F0.wireOp",EDGE,"E6.2.14.0"),sQuery(id+"F0.wireOp",EDGE,"E6.2.15.0"),sQuery(id+"F0.wireOp",EDGE,"E6.3.0.0"),sQuery(id+"F0.wireOp",EDGE,"E6.3.1.0"),sQuery(id+"F0.wireOp",EDGE,"E6.3.2.0"),sQuery(id+"F0.wireOp",EDGE,"E6.3.3.0"),sQuery(id+"F0.wireOp",EDGE,"E6.3.4.0"),sQuery(id+"F0.wireOp",EDGE,"E6.3.5.0"),sQuery(id+"F0.wireOp",EDGE,"E6.3.6.0"),sQuery(id+"F0.wireOp",EDGE,"E6.3.7.0"),sQuery(id+"F0.wireOp",EDGE,"E6.3.8.0"),sQuery(id+"F0.wireOp",EDGE,"E6.3.9.0"),sQuery(id+"F0.wireOp",EDGE,"E6.3.10.0"),sQuery(id+"F0.wireOp",EDGE,"E6.3.11.0"),sQuery(id+"F0.wireOp",EDGE,"E6.3.12.0"),sQuery(id+"F0.wireOp",EDGE,"E6.3.13.0"),sQuery(id+"F0.wireOp",EDGE,"E6.3.14.0"),sQuery(id+"F0.wireOp",EDGE,"E6.3.15.0"),sQuery(id+"F0.wireOp",EDGE,"E6.4.0.0"),sQuery(id+"F0.wireOp",EDGE,"E6.4.1.0"),sQuery(id+"F0.wireOp",EDGE,"E6.4.2.0"),sQuery(id+"F0.wireOp",EDGE,"E6.4.3.0"),sQuery(id+"F0.wireOp",EDGE,"E6.4.4.0"),sQuery(id+"F0.wireOp",EDGE,"E6.4.5.0"),sQuery(id+"F0.wireOp",EDGE,"E6.4.6.0"),sQuery(id+"F0.wireOp",EDGE,"E6.4.7.0"),sQuery(id+"F0.wireOp",EDGE,"E6.4.8.0"),sQuery(id+"F0.wireOp",EDGE,"E6.4.9.0"),sQuery(id+"F0.wireOp",EDGE,"E6.4.10.0"),sQuery(id+"F0.wireOp",EDGE,"E6.4.11.0"),sQuery(id+"F0.wireOp",EDGE,"E6.4.12.0"),sQuery(id+"F0.wireOp",EDGE,"E6.4.13.0"),sQuery(id+"F0.wireOp",EDGE,"E6.4.14.0"),sQuery(id+"F0.wireOp",EDGE,"E6.4.15.0"),sQuery(id+"F0.wireOp",EDGE,"E6.5.0.0"),sQuery(id+"F0.wireOp",EDGE,"E6.5.1.0"),sQuery(id+"F0.wireOp",EDGE,"E6.5.2.0"),sQuery(id+"F0.wireOp",EDGE,"E6.5.3.0"),sQuery(id+"F0.wireOp",EDGE,"E6.5.4.0"),sQuery(id+"F0.wireOp",EDGE,"E6.5.5.0"),sQuery(id+"F0.wireOp",EDGE,"E6.5.6.0"),sQuery(id+"F0.wireOp",EDGE,"E6.5.7.0"),sQuery(id+"F0.wireOp",EDGE,"E6.5.8.0"),sQuery(id+"F0.wireOp",EDGE,"E6.5.9.0"),sQuery(id+"F0.wireOp",EDGE,"E6.5.10.0"),sQuery(id+"F0.wireOp",EDGE,"E6.5.11.0"),sQuery(id+"F0.wireOp",EDGE,"E6.5.12.0"),sQuery(id+"F0.wireOp",EDGE,"E6.5.13.0"),sQuery(id+"F0.wireOp",EDGE,"E6.5.14.0"),sQuery(id+"F0.wireOp",EDGE,"E6.5.15.0"),sQuery(id+"F0.wireOp",EDGE,"E6.6.0.0"),sQuery(id+"F0.wireOp",EDGE,"E6.6.1.0"),sQuery(id+"F0.wireOp",EDGE,"E6.6.2.0"),sQuery(id+"F0.wireOp",EDGE,"E6.6.3.0"),sQuery(id+"F0.wireOp",EDGE,"E6.6.4.0"),sQuery(id+"F0.wireOp",EDGE,"E6.6.5.0"),sQuery(id+"F0.wireOp",EDGE,"E6.6.6.0"),sQuery(id+"F0.wireOp",EDGE,"E6.6.7.0"),sQuery(id+"F0.wireOp",EDGE,"E6.6.8.0"),sQuery(id+"F0.wireOp",EDGE,"E6.6.9.0"),sQuery(id+"F0.wireOp",EDGE,"E6.6.10.0"),sQuery(id+"F0.wireOp",EDGE,"E6.6.11.0"),sQuery(id+"F0.wireOp",EDGE,"E6.6.12.0"),sQuery(id+"F0.wireOp",EDGE,"E6.6.13.0"),sQuery(id+"F0.wireOp",EDGE,"E6.6.14.0"),sQuery(id+"F0.wireOp",EDGE,"E6.6.15.0"),sQuery(id+"F0.wireOp",EDGE,"E6.7.0.0"),sQuery(id+"F0.wireOp",EDGE,"E6.7.1.0"),sQuery(id+"F0.wireOp",EDGE,"E6.7.2.0"),sQuery(id+"F0.wireOp",EDGE,"E6.7.3.0"),sQuery(id+"F0.wireOp",EDGE,"E6.7.4.0"),sQuery(id+"F0.wireOp",EDGE,"E6.7.5.0"),sQuery(id+"F0.wireOp",EDGE,"E6.7.6.0"),sQuery(id+"F0.wireOp",EDGE,"E6.7.7.0"),sQuery(id+"F0.wireOp",EDGE,"E6.7.8.0"),sQuery(id+"F0.wireOp",EDGE,"E6.7.9.0"),sQuery(id+"F0.wireOp",EDGE,"E6.7.10.0"),sQuery(id+"F0.wireOp",EDGE,"E6.7.11.0"),sQuery(id+"F0.wireOp",EDGE,"E6.7.12.0"),sQuery(id+"F0.wireOp",EDGE,"E6.7.13.0"),sQuery(id+"F0.wireOp",EDGE,"E6.7.14.0"),sQuery(id+"F0.wireOp",EDGE,"E6.7.15.0"),sQuery(id+"F0.wireOp",EDGE,"E6.8.0.0"),sQuery(id+"F0.wireOp",EDGE,"E6.8.1.0"),sQuery(id+"F0.wireOp",EDGE,"E6.8.2.0"),sQuery(id+"F0.wireOp",EDGE,"E6.8.3.0"),sQuery(id+"F0.wireOp",EDGE,"E6.8.4.0"),sQuery(id+"F0.wireOp",EDGE,"E6.8.5.0"),sQuery(id+"F0.wireOp",EDGE,"E6.8.6.0"),sQuery(id+"F0.wireOp",EDGE,"E6.8.7.0"),sQuery(id+"F0.wireOp",EDGE,"E6.8.8.0"),sQuery(id+"F0.wireOp",EDGE,"E6.8.9.0"),sQuery(id+"F0.wireOp",EDGE,"E6.8.10.0"),sQuery(id+"F0.wireOp",EDGE,"E6.8.11.0"),sQuery(id+"F0.wireOp",EDGE,"E6.8.12.0"),sQuery(id+"F0.wireOp",EDGE,"E6.8.13.0"),sQuery(id+"F0.wireOp",EDGE,"E6.8.14.0"),sQuery(id+"F0.wireOp",EDGE,"E6.8.15.0"),sQuery(id+"F0.wireOp",EDGE,"E6.9.0.0"),sQuery(id+"F0.wireOp",EDGE,"E6.9.1.0"),sQuery(id+"F0.wireOp",EDGE,"E6.9.2.0"),sQuery(id+"F0.wireOp",EDGE,"E6.9.3.0"),sQuery(id+"F0.wireOp",EDGE,"E6.9.4.0"),sQuery(id+"F0.wireOp",EDGE,"E6.9.5.0"),sQuery(id+"F0.wireOp",EDGE,"E6.9.6.0"),sQuery(id+"F0.wireOp",EDGE,"E6.9.7.0"),sQuery(id+"F0.wireOp",EDGE,"E6.9.8.0"),sQuery(id+"F0.wireOp",EDGE,"E6.9.9.0"),sQuery(id+"F0.wireOp",EDGE,"E6.9.10.0"),sQuery(id+"F0.wireOp",EDGE,"E6.9.11.0"),sQuery(id+"F0.wireOp",EDGE,"E6.9.12.0"),sQuery(id+"F0.wireOp",EDGE,"E6.9.13.0"),sQuery(id+"F0.wireOp",EDGE,"E6.9.14.0"),sQuery(id+"F0.wireOp",EDGE,"E6.9.15.0"),sQuery(id+"F0.wireOp",EDGE,"E6.10.0.0"),sQuery(id+"F0.wireOp",EDGE,"E6.10.1.0"),sQuery(id+"F0.wireOp",EDGE,"E6.10.2.0"),sQuery(id+"F0.wireOp",EDGE,"E6.10.3.0"),sQuery(id+"F0.wireOp",EDGE,"E6.10.4.0"),sQuery(id+"F0.wireOp",EDGE,"E6.10.5.0"),sQuery(id+"F0.wireOp",EDGE,"E6.10.6.0"),sQuery(id+"F0.wireOp",EDGE,"E6.10.7.0"),sQuery(id+"F0.wireOp",EDGE,"E6.10.8.0"),sQuery(id+"F0.wireOp",EDGE,"E6.10.9.0"),sQuery(id+"F0.wireOp",EDGE,"E6.10.10.0"),sQuery(id+"F0.wireOp",EDGE,"E6.10.11.0"),sQuery(id+"F0.wireOp",EDGE,"E6.10.12.0"),sQuery(id+"F0.wireOp",EDGE,"E6.10.13.0"),sQuery(id+"F0.wireOp",EDGE,"E6.10.14.0"),sQuery(id+"F0.wireOp",EDGE,"E6.10.15.0"),sQuery(id+"F0.wireOp",EDGE,"E6.11.0.0"),sQuery(id+"F0.wireOp",EDGE,"E6.11.1.0"),sQuery(id+"F0.wireOp",EDGE,"E6.11.2.0"),sQuery(id+"F0.wireOp",EDGE,"E6.11.3.0"),sQuery(id+"F0.wireOp",EDGE,"E6.11.4.0"),sQuery(id+"F0.wireOp",EDGE,"E6.11.5.0"),sQuery(id+"F0.wireOp",EDGE,"E6.11.6.0"),sQuery(id+"F0.wireOp",EDGE,"E6.11.7.0"),sQuery(id+"F0.wireOp",EDGE,"E6.11.8.0"),sQuery(id+"F0.wireOp",EDGE,"E6.11.9.0"),sQuery(id+"F0.wireOp",EDGE,"E6.11.10.0"),sQuery(id+"F0.wireOp",EDGE,"E6.11.11.0"),sQuery(id+"F0.wireOp",EDGE,"E6.11.12.0"),sQuery(id+"F0.wireOp",EDGE,"E6.11.13.0"),sQuery(id+"F0.wireOp",EDGE,"E6.11.14.0"),sQuery(id+"F0.wireOp",EDGE,"E6.11.15.0"),sQuery(id+"F0.wireOp",EDGE,"E6.12.0.0"),sQuery(id+"F0.wireOp",EDGE,"E6.12.1.0"),sQuery(id+"F0.wireOp",EDGE,"E6.12.2.0"),sQuery(id+"F0.wireOp",EDGE,"E6.12.3.0"),sQuery(id+"F0.wireOp",EDGE,"E6.12.4.0"),sQuery(id+"F0.wireOp",EDGE,"E6.12.5.0"),sQuery(id+"F0.wireOp",EDGE,"E6.12.6.0"),sQuery(id+"F0.wireOp",EDGE,"E6.12.7.0"),sQuery(id+"F0.wireOp",EDGE,"E6.12.8.0"),sQuery(id+"F0.wireOp",EDGE,"E6.12.9.0"),sQuery(id+"F0.wireOp",EDGE,"E6.12.10.0"),sQuery(id+"F0.wireOp",EDGE,"E6.12.11.0"),sQuery(id+"F0.wireOp",EDGE,"E6.12.12.0"),sQuery(id+"F0.wireOp",EDGE,"E6.12.13.0"),sQuery(id+"F0.wireOp",EDGE,"E6.12.14.0"),sQuery(id+"F0.wireOp",EDGE,"E6.12.15.0"),sQuery(id+"F0.wireOp",EDGE,"E6.13.0.0"),sQuery(id+"F0.wireOp",EDGE,"E6.13.1.0"),sQuery(id+"F0.wireOp",EDGE,"E6.13.2.0"),sQuery(id+"F0.wireOp",EDGE,"E6.13.3.0"),sQuery(id+"F0.wireOp",EDGE,"E6.13.4.0"),sQuery(id+"F0.wireOp",EDGE,"E6.13.5.0"),sQuery(id+"F0.wireOp",EDGE,"E6.13.6.0"),sQuery(id+"F0.wireOp",EDGE,"E6.13.7.0"),sQuery(id+"F0.wireOp",EDGE,"E6.13.8.0"),sQuery(id+"F0.wireOp",EDGE,"E6.13.9.0"),sQuery(id+"F0.wireOp",EDGE,"E6.13.10.0"),sQuery(id+"F0.wireOp",EDGE,"E6.13.11.0"),sQuery(id+"F0.wireOp",EDGE,"E6.13.12.0"),sQuery(id+"F0.wireOp",EDGE,"E6.13.13.0"),sQuery(id+"F0.wireOp",EDGE,"E6.13.14.0"),sQuery(id+"F0.wireOp",EDGE,"E6.13.15.0"),sQuery(id+"F0.wireOp",EDGE,"E6.14.0.0"),sQuery(id+"F0.wireOp",EDGE,"E6.14.1.0"),sQuery(id+"F0.wireOp",EDGE,"E6.14.2.0"),sQuery(id+"F0.wireOp",EDGE,"E6.14.3.0"),sQuery(id+"F0.wireOp",EDGE,"E6.14.4.0"),sQuery(id+"F0.wireOp",EDGE,"E6.14.5.0"),sQuery(id+"F0.wireOp",EDGE,"E6.14.6.0"),sQuery(id+"F0.wireOp",EDGE,"E6.14.7.0"),sQuery(id+"F0.wireOp",EDGE,"E6.14.8.0"),sQuery(id+"F0.wireOp",EDGE,"E6.14.9.0"),sQuery(id+"F0.wireOp",EDGE,"E6.14.10.0"),sQuery(id+"F0.wireOp",EDGE,"E6.14.11.0"),sQuery(id+"F0.wireOp",EDGE,"E6.14.12.0"),sQuery(id+"F0.wireOp",EDGE,"E6.14.13.0"),sQuery(id+"F0.wireOp",EDGE,"E6.14.14.0"),sQuery(id+"F0.wireOp",EDGE,"E6.14.15.0"),sQuery(id+"F0.wireOp",EDGE,"E6.15.0.0"),sQuery(id+"F0.wireOp",EDGE,"E6.15.1.0"),sQuery(id+"F0.wireOp",EDGE,"E6.15.2.0"),sQuery(id+"F0.wireOp",EDGE,"E6.15.3.0"),sQuery(id+"F0.wireOp",EDGE,"E6.15.4.0"),sQuery(id+"F0.wireOp",EDGE,"E6.15.5.0"),sQuery(id+"F0.wireOp",EDGE,"E6.15.6.0"),sQuery(id+"F0.wireOp",EDGE,"E6.15.7.0"),sQuery(id+"F0.wireOp",EDGE,"E6.15.8.0"),sQuery(id+"F0.wireOp",EDGE,"E6.15.9.0"),sQuery(id+"F0.wireOp",EDGE,"E6.15.10.0"),sQuery(id+"F0.wireOp",EDGE,"E6.15.11.0"),sQuery(id+"F0.wireOp",EDGE,"E6.15.12.0"),sQuery(id+"F0.wireOp",EDGE,"E6.15.13.0"),sQuery(id+"F0.wireOp",EDGE,"E6.15.14.0"),sQuery(id+"F0.wireOp",EDGE,"E6.15.15.0"),sQuery(id+"F0.wireOp",EDGE,"E7.0.0.16"),sQuery(id+"F0.wireOp",EDGE,"E7.0.0.17"),sQuery(id+"F0.wireOp",EDGE,"E7.0.0.18"),sQuery(id+"F0.wireOp",EDGE,"E7.0.0.19"),sQuery(id+"F0.wireOp",EDGE,"E7.0.1.16"),sQuery(id+"F0.wireOp",EDGE,"E7.0.1.17"),sQuery(id+"F0.wireOp",EDGE,"E7.0.1.18"),sQuery(id+"F0.wireOp",EDGE,"E7.0.1.19"),sQuery(id+"F0.wireOp",EDGE,"E7.0.2.16"),sQuery(id+"F0.wireOp",EDGE,"E7.0.2.17"),sQuery(id+"F0.wireOp",EDGE,"E7.0.2.18"),sQuery(id+"F0.wireOp",EDGE,"E7.0.2.19"),sQuery(id+"F0.wireOp",EDGE,"E7.0.3.16"),sQuery(id+"F0.wireOp",EDGE,"E7.0.3.17"),sQuery(id+"F0.wireOp",EDGE,"E7.0.3.18"),sQuery(id+"F0.wireOp",EDGE,"E7.0.3.19"),sQuery(id+"F0.wireOp",EDGE,"E7.0.4.16"),sQuery(id+"F0.wireOp",EDGE,"E7.0.4.17"),sQuery(id+"F0.wireOp",EDGE,"E7.0.4.18"),sQuery(id+"F0.wireOp",EDGE,"E7.0.4.19"),sQuery(id+"F0.wireOp",EDGE,"E7.0.5.16"),sQuery(id+"F0.wireOp",EDGE,"E7.0.5.17"),sQuery(id+"F0.wireOp",EDGE,"E7.0.5.18"),sQuery(id+"F0.wireOp",EDGE,"E7.0.5.19"),sQuery(id+"F0.wireOp",EDGE,"E7.0.6.16"),sQuery(id+"F0.wireOp",EDGE,"E7.0.6.17"),sQuery(id+"F0.wireOp",EDGE,"E7.0.6.18"),sQuery(id+"F0.wireOp",EDGE,"E7.0.6.19"),sQuery(id+"F0.wireOp",EDGE,"E7.0.7.16"),sQuery(id+"F0.wireOp",EDGE,"E7.0.7.17"),sQuery(id+"F0.wireOp",EDGE,"E7.0.7.18"),sQuery(id+"F0.wireOp",EDGE,"E7.0.7.19"),sQuery(id+"F0.wireOp",EDGE,"E7.0.8.16"),sQuery(id+"F0.wireOp",EDGE,"E7.0.8.17"),sQuery(id+"F0.wireOp",EDGE,"E7.0.8.18"),sQuery(id+"F0.wireOp",EDGE,"E7.0.8.19"),sQuery(id+"F0.wireOp",EDGE,"E7.0.9.16"),sQuery(id+"F0.wireOp",EDGE,"E7.0.9.17"),sQuery(id+"F0.wireOp",EDGE,"E7.0.9.18"),sQuery(id+"F0.wireOp",EDGE,"E7.0.9.19"),sQuery(id+"F0.wireOp",EDGE,"E7.0.10.16"),sQuery(id+"F0.wireOp",EDGE,"E7.0.10.17"),sQuery(id+"F0.wireOp",EDGE,"E7.0.10.18"),sQuery(id+"F0.wireOp",EDGE,"E7.0.10.19"),sQuery(id+"F0.wireOp",EDGE,"E7.0.11.16"),sQuery(id+"F0.wireOp",EDGE,"E7.0.11.17"),sQuery(id+"F0.wireOp",EDGE,"E7.0.11.18"),sQuery(id+"F0.wireOp",EDGE,"E7.0.11.19"),sQuery(id+"F0.wireOp",EDGE,"E7.0.12.16"),sQuery(id+"F0.wireOp",EDGE,"E7.0.12.17"),sQuery(id+"F0.wireOp",EDGE,"E7.0.12.18"),sQuery(id+"F0.wireOp",EDGE,"E7.0.12.19"),sQuery(id+"F0.wireOp",EDGE,"E7.0.13.16"),sQuery(id+"F0.wireOp",EDGE,"E7.0.13.17"),sQuery(id+"F0.wireOp",EDGE,"E7.0.13.18"),sQuery(id+"F0.wireOp",EDGE,"E7.0.13.19"),sQuery(id+"F0.wireOp",EDGE,"E7.0.14.16"),sQuery(id+"F0.wireOp",EDGE,"E7.0.14.17"),sQuery(id+"F0.wireOp",EDGE,"E7.0.14.18"),sQuery(id+"F0.wireOp",EDGE,"E7.0.14.19"),sQuery(id+"F0.wireOp",EDGE,"E7.0.15.16"),sQuery(id+"F0.wireOp",EDGE,"E7.0.15.17"),sQuery(id+"F0.wireOp",EDGE,"E7.0.15.18"),sQuery(id+"F0.wireOp",EDGE,"E7.0.15.19"),sQuery(id+"F0.wireOp",EDGE,"E8.0.16.0"),sQuery(id+"F0.wireOp",EDGE,"E8.0.16.1"),sQuery(id+"F0.wireOp",EDGE,"E8.0.16.2"),sQuery(id+"F0.wireOp",EDGE,"E8.0.16.3"),sQuery(id+"F0.wireOp",EDGE,"E8.0.16.4"),sQuery(id+"F0.wireOp",EDGE,"E8.0.16.5"),sQuery(id+"F0.wireOp",EDGE,"E8.0.16.6"),sQuery(id+"F0.wireOp",EDGE,"E8.0.16.7"),sQuery(id+"F0.wireOp",EDGE,"E8.0.16.8"),sQuery(id+"F0.wireOp",EDGE,"E8.0.16.9"),sQuery(id+"F0.wireOp",EDGE,"E8.0.16.10"),sQuery(id+"F0.wireOp",EDGE,"E8.0.16.11"),sQuery(id+"F0.wireOp",EDGE,"E8.0.16.12"),sQuery(id+"F0.wireOp",EDGE,"E8.0.16.13"),sQuery(id+"F0.wireOp",EDGE,"E8.0.16.14"),sQuery(id+"F0.wireOp",EDGE,"E8.0.16.15"),sQuery(id+"F0.wireOp",EDGE,"E8.0.16.16"),sQuery(id+"F0.wireOp",EDGE,"E8.0.16.17"),sQuery(id+"F0.wireOp",EDGE,"E8.0.16.18"),sQuery(id+"F0.wireOp",EDGE,"E8.0.16.19"),sQuery(id+"F0.wireOp",EDGE,"E8.0.17.0"),sQuery(id+"F0.wireOp",EDGE,"E8.0.17.1"),sQuery(id+"F0.wireOp",EDGE,"E8.0.17.2"),sQuery(id+"F0.wireOp",EDGE,"E8.0.17.3"),sQuery(id+"F0.wireOp",EDGE,"E8.0.17.4"),sQuery(id+"F0.wireOp",EDGE,"E8.0.17.5"),sQuery(id+"F0.wireOp",EDGE,"E8.0.17.6"),sQuery(id+"F0.wireOp",EDGE,"E8.0.17.7"),sQuery(id+"F0.wireOp",EDGE,"E8.0.17.8"),sQuery(id+"F0.wireOp",EDGE,"E8.0.17.9"),sQuery(id+"F0.wireOp",EDGE,"E8.0.17.10"),sQuery(id+"F0.wireOp",EDGE,"E8.0.17.11"),sQuery(id+"F0.wireOp",EDGE,"E8.0.17.12"),sQuery(id+"F0.wireOp",EDGE,"E8.0.17.13"),sQuery(id+"F0.wireOp",EDGE,"E8.0.17.14"),sQuery(id+"F0.wireOp",EDGE,"E8.0.17.15"),sQuery(id+"F0.wireOp",EDGE,"E8.0.17.16"),sQuery(id+"F0.wireOp",EDGE,"E8.0.17.17"),sQuery(id+"F0.wireOp",EDGE,"E8.0.17.18"),sQuery(id+"F0.wireOp",EDGE,"E8.0.17.19"),sQuery(id+"F0.wireOp",EDGE,"E8.0.18.0"),sQuery(id+"F0.wireOp",EDGE,"E8.0.18.1"),sQuery(id+"F0.wireOp",EDGE,"E8.0.18.2"),sQuery(id+"F0.wireOp",EDGE,"E8.0.18.3"),sQuery(id+"F0.wireOp",EDGE,"E8.0.18.4"),sQuery(id+"F0.wireOp",EDGE,"E8.0.18.5"),sQuery(id+"F0.wireOp",EDGE,"E8.0.18.6"),sQuery(id+"F0.wireOp",EDGE,"E8.0.18.7"),sQuery(id+"F0.wireOp",EDGE,"E8.0.18.8"),sQuery(id+"F0.wireOp",EDGE,"E8.0.18.9"),sQuery(id+"F0.wireOp",EDGE,"E8.0.18.10"),sQuery(id+"F0.wireOp",EDGE,"E8.0.18.11"),sQuery(id+"F0.wireOp",EDGE,"E8.0.18.12"),sQuery(id+"F0.wireOp",EDGE,"E8.0.18.13"),sQuery(id+"F0.wireOp",EDGE,"E8.0.18.14"),sQuery(id+"F0.wireOp",EDGE,"E8.0.18.15"),sQuery(id+"F0.wireOp",EDGE,"E8.0.18.16"),sQuery(id+"F0.wireOp",EDGE,"E8.0.18.17"),sQuery(id+"F0.wireOp",EDGE,"E8.0.18.18"),sQuery(id+"F0.wireOp",EDGE,"E8.0.18.19"),sQuery(id+"F0.wireOp",EDGE,"E8.0.19.0"),sQuery(id+"F0.wireOp",EDGE,"E8.0.19.1"),sQuery(id+"F0.wireOp",EDGE,"E8.0.19.2"),sQuery(id+"F0.wireOp",EDGE,"E8.0.19.3"),sQuery(id+"F0.wireOp",EDGE,"E8.0.19.4"),sQuery(id+"F0.wireOp",EDGE,"E8.0.19.5"),sQuery(id+"F0.wireOp",EDGE,"E8.0.19.6"),sQuery(id+"F0.wireOp",EDGE,"E8.0.19.7"),sQuery(id+"F0.wireOp",EDGE,"E8.0.19.8"),sQuery(id+"F0.wireOp",EDGE,"E8.0.19.9"),sQuery(id+"F0.wireOp",EDGE,"E8.0.19.10"),sQuery(id+"F0.wireOp",EDGE,"E8.0.19.11"),sQuery(id+"F0.wireOp",EDGE,"E8.0.19.12"),sQuery(id+"F0.wireOp",EDGE,"E8.0.19.13"),sQuery(id+"F0.wireOp",EDGE,"E8.0.19.14"),sQuery(id+"F0.wireOp",EDGE,"E8.0.19.15"),sQuery(id+"F0.wireOp",EDGE,"E8.0.19.16"),sQuery(id+"F0.wireOp",EDGE,"E8.0.19.17"),sQuery(id+"F0.wireOp",EDGE,"E8.0.19.18"),sQuery(id+"F0.wireOp",EDGE,"E8.0.19.19")])],"isStart":false});
            var sketch = newSketch(context, id + "F2", { "sketchPlane" : qUnion([Q0])});
            skCircle(sketch, "E9", {"center": v(20, 250) * mm, "radius": 4.75 * mm});
            skCircle(sketch, "E10", {"center": v(250, 250) * mm, "radius": 4.75 * mm});
            skCircle(sketch, "E11", {"center": v(20, 20) * mm, "radius": 4.75 * mm});
            skCircle(sketch, "E12", {"center": v(250, 20) * mm, "radius": 4.75 * mm});
            skSolve(sketch);
        }
        {
            var Q0;
            Q0=makeQuery(id+"F2.imprint","IMPRINT",FACE,{"disambiguationData":[TD([[makeQuery(id+"F2.imprint","IMPRINT",EDGE,{"derivedFrom":sQuery(id+"F2.wireOp",EDGE,"E11")}),1.0]])]});
            var Q1;
            Q1=makeQuery(id+"F2.imprint","IMPRINT",FACE,{"disambiguationData":[TD([[makeQuery(id+"F2.imprint","IMPRINT",EDGE,{"derivedFrom":sQuery(id+"F2.wireOp",EDGE,"E9")}),1.0]])]});
            var Q2;
            Q2=makeQuery(id+"F2.imprint","IMPRINT",FACE,{"disambiguationData":[TD([[makeQuery(id+"F2.imprint","IMPRINT",EDGE,{"derivedFrom":sQuery(id+"F2.wireOp",EDGE,"E10")}),1.0]])]});
            var Q3;
            Q3=makeQuery(id+"F2.imprint","IMPRINT",FACE,{"disambiguationData":[TD([[makeQuery(id+"F2.imprint","IMPRINT",EDGE,{"derivedFrom":sQuery(id+"F2.wireOp",EDGE,"E12")}),1.0]])]});
            extrude(context, id + "F3", {"entities" : qUnion([Q0, Q1, Q2, Q3]), "operationType" : NewBodyOperationType.REMOVE, "oppositeDirection" : true, "depth" : 5.5 * mm});
        }
        {
            var Q0;
            Q0=makeQuery(id+"F0.imprint","IMPRINT",FACE,{"disambiguationData":[TD([[makeQuery(id+"F0.imprint","IMPRINT",EDGE,{"derivedFrom":sQuery(id+"F0.wireOp",EDGE,"E0.bottom")}),1.0]])]});
            var sketch = newSketch(context, id + "F4", { "sketchPlane" : qUnion([Q0])});
            skCircle(sketch, "E13", {"center": v(66, 20) * mm, "radius": 1.75 * mm});
            skCircle(sketch, "E14.1.0.0", {"center": v(112, 20) * mm, "radius": 1.75 * mm});
            skCircle(sketch, "E14.2.0.0", {"center": v(158, 20) * mm, "radius": 1.75 * mm});
            skCircle(sketch, "E14.3.0.0", {"center": v(204, 20) * mm, "radius": 1.75 * mm});
            skLineSegment(sketch, "E14.direction1", {"start": v(66, 20) * mm, "end": v(112, 20) * mm, "construction": true});
            skCircle(sketch, "E15", {"center": v(20, 66) * mm, "radius": 1.75 * mm});
            skCircle(sketch, "E16.0.1.0", {"center": v(20, 112) * mm, "radius": 1.75 * mm});
            skCircle(sketch, "E16.0.2.0", {"center": v(20, 158) * mm, "radius": 1.75 * mm});
            skCircle(sketch, "E16.0.3.0", {"center": v(20, 204) * mm, "radius": 1.75 * mm});
            skLineSegment(sketch, "E16.direction1", {"start": v(20, 66) * mm, "end": v(45, 66) * mm, "construction": true});
            skLineSegment(sketch, "E16.direction2", {"start": v(20, 66) * mm, "end": v(20, 112) * mm, "construction": true});
            skCircle(sketch, "E17", {"center": v(66, 250) * mm, "radius": 1.75 * mm});
            skCircle(sketch, "E18.1.0.0", {"center": v(112, 250) * mm, "radius": 1.75 * mm});
            skCircle(sketch, "E18.2.0.0", {"center": v(158, 250) * mm, "radius": 1.75 * mm});
            skCircle(sketch, "E18.3.0.0", {"center": v(204, 250) * mm, "radius": 1.75 * mm});
            skLineSegment(sketch, "E18.direction1", {"start": v(66, 250) * mm, "end": v(112, 250) * mm, "construction": true});
            skCircle(sketch, "E19", {"center": v(250, 66) * mm, "radius": 1.75 * mm});
            skCircle(sketch, "E20.0.1.0", {"center": v(250, 112) * mm, "radius": 1.75 * mm});
            skCircle(sketch, "E20.0.2.0", {"center": v(250, 158) * mm, "radius": 1.75 * mm});
            skCircle(sketch, "E20.0.3.0", {"center": v(250, 204) * mm, "radius": 1.75 * mm});
            skLineSegment(sketch, "E20.direction1", {"start": v(250, 66) * mm, "end": v(275, 66) * mm, "construction": true});
            skLineSegment(sketch, "E20.direction2", {"start": v(250, 66) * mm, "end": v(250, 112) * mm, "construction": true});
            skSolve(sketch);
        }
        {
            var Q0;
            Q0=makeQuery(id+"F4.imprint","IMPRINT",FACE,{"disambiguationData":[TD([[makeQuery(id+"F4.imprint","IMPRINT",EDGE,{"derivedFrom":sQuery(id+"F4.wireOp",EDGE,"E15")}),1.0]])]});
            var Q1;
            Q1=makeQuery(id+"F4.imprint","IMPRINT",FACE,{"disambiguationData":[TD([[makeQuery(id+"F4.imprint","IMPRINT",EDGE,{"derivedFrom":sQuery(id+"F4.wireOp",EDGE,"E13")}),1.0]])]});
            var Q2;
            Q2=makeQuery(id+"F4.imprint","IMPRINT",FACE,{"disambiguationData":[TD([[makeQuery(id+"F4.imprint","IMPRINT",EDGE,{"derivedFrom":sQuery(id+"F4.wireOp",EDGE,"E14.1.0.0")}),1.0]])]});
            var Q3;
            Q3=makeQuery(id+"F4.imprint","IMPRINT",FACE,{"disambiguationData":[TD([[makeQuery(id+"F4.imprint","IMPRINT",EDGE,{"derivedFrom":sQuery(id+"F4.wireOp",EDGE,"E14.2.0.0")}),1.0]])]});
            var Q4;
            Q4=makeQuery(id+"F4.imprint","IMPRINT",FACE,{"disambiguationData":[TD([[makeQuery(id+"F4.imprint","IMPRINT",EDGE,{"derivedFrom":sQuery(id+"F4.wireOp",EDGE,"E14.3.0.0")}),1.0]])]});
            var Q5;
            Q5=makeQuery(id+"F4.imprint","IMPRINT",FACE,{"disambiguationData":[TD([[makeQuery(id+"F4.imprint","IMPRINT",EDGE,{"derivedFrom":sQuery(id+"F4.wireOp",EDGE,"E19")}),1.0]])]});
            var Q6;
            Q6=makeQuery(id+"F4.imprint","IMPRINT",FACE,{"disambiguationData":[TD([[makeQuery(id+"F4.imprint","IMPRINT",EDGE,{"derivedFrom":sQuery(id+"F4.wireOp",EDGE,"E20.0.1.0")}),1.0]])]});
            var Q7;
            Q7=makeQuery(id+"F4.imprint","IMPRINT",FACE,{"disambiguationData":[TD([[makeQuery(id+"F4.imprint","IMPRINT",EDGE,{"derivedFrom":sQuery(id+"F4.wireOp",EDGE,"E20.0.2.0")}),1.0]])]});
            var Q8;
            Q8=makeQuery(id+"F4.imprint","IMPRINT",FACE,{"disambiguationData":[TD([[makeQuery(id+"F4.imprint","IMPRINT",EDGE,{"derivedFrom":sQuery(id+"F4.wireOp",EDGE,"E20.0.3.0")}),1.0]])]});
            var Q9;
            Q9=makeQuery(id+"F4.imprint","IMPRINT",FACE,{"disambiguationData":[TD([[makeQuery(id+"F4.imprint","IMPRINT",EDGE,{"derivedFrom":sQuery(id+"F4.wireOp",EDGE,"E18.3.0.0")}),1.0]])]});
            var Q10;
            Q10=makeQuery(id+"F4.imprint","IMPRINT",FACE,{"disambiguationData":[TD([[makeQuery(id+"F4.imprint","IMPRINT",EDGE,{"derivedFrom":sQuery(id+"F4.wireOp",EDGE,"E18.2.0.0")}),1.0]])]});
            var Q11;
            Q11=makeQuery(id+"F4.imprint","IMPRINT",FACE,{"disambiguationData":[TD([[makeQuery(id+"F4.imprint","IMPRINT",EDGE,{"derivedFrom":sQuery(id+"F4.wireOp",EDGE,"E18.1.0.0")}),1.0]])]});
            var Q12;
            Q12=makeQuery(id+"F4.imprint","IMPRINT",FACE,{"disambiguationData":[TD([[makeQuery(id+"F4.imprint","IMPRINT",EDGE,{"derivedFrom":sQuery(id+"F4.wireOp",EDGE,"E17")}),1.0]])]});
            var Q13;
            Q13=makeQuery(id+"F4.imprint","IMPRINT",FACE,{"disambiguationData":[TD([[makeQuery(id+"F4.imprint","IMPRINT",EDGE,{"derivedFrom":sQuery(id+"F4.wireOp",EDGE,"E16.0.3.0")}),1.0]])]});
            var Q14;
            Q14=makeQuery(id+"F4.imprint","IMPRINT",FACE,{"disambiguationData":[TD([[makeQuery(id+"F4.imprint","IMPRINT",EDGE,{"derivedFrom":sQuery(id+"F4.wireOp",EDGE,"E16.0.2.0")}),1.0]])]});
            var Q15;
            Q15=makeQuery(id+"F4.imprint","IMPRINT",FACE,{"disambiguationData":[TD([[makeQuery(id+"F4.imprint","IMPRINT",EDGE,{"derivedFrom":sQuery(id+"F4.wireOp",EDGE,"E16.0.1.0")}),1.0]])]});
            extrude(context, id + "F5", {"entities" : qUnion([Q0, Q1, Q2, Q3, Q4, Q5, Q6, Q7, Q8, Q9, Q10, Q11, Q12, Q13, Q14, Q15]), "operationType" : NewBodyOperationType.REMOVE, "depth" : 8 * mm});
        }
    });
